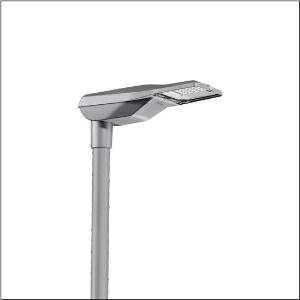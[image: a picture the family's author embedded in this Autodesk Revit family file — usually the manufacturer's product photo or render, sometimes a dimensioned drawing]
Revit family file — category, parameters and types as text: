
# Revit family: streetlight_sl_21_iq_micro___st1_5a_5xe1p31d08cb_2d79
name_source: partatom
category: Lighting Fixtures
units: mm (PartAtom-declared; Revit-internal decimal feet)

## family parameters
Cut with Voids When Loaded = No
Host = Face
Light Source = No
Part Type = Normal
Room Calculation Point = No
Round Connector Dimension = Use Diameter
Shared = No

## types (1)
- --- (1 x LED, 2820 lm, 19.4 W, 3000K)
    Apparent Load = 19 VA
    CIE Flux Codes = 22 53 95 100 100
    Color Rendering = 70
    Color Temperature = 3000K
    Default Elevation = 1800 mm
    Description = Streetlight SL 21 iQ micro, mast luminaire, primary light control with lens, of PMMA, primary optical cover: cover, of toughened safety glass, transparent, light distribution: ST1.5a, light emission: direct distribution, primary light characteristic: asymmetric, installation type: post-top, side-entry, LED, High Power LED, rated luminous flux: 2.820lm, luminous efficacy: 145lm/W, light colour: 730, colour temperature: 3000K, control: Auto-Match, Temp-Guard, Lumen-Switch, Night-Set, Smart-Wire, Light-Fading, Desk-Remote (wireless, voltage-free reading and setting of iQ features in the workshop via application-optimized NFC function/RFID function), optimised constant luminous flux control (CLO 2.0), pre-setting: linear dimming characteristic, mains connection: 220..240V, AC, 50/60Hz, start of lifetime: 19W, end of service life: 20W, reduction: 10W, luminaire housing, of diecast aluminium, powder-coated, Siteco® metallic grey (DB 702S), corrosivity category C5 mid according to DIN EN ISO 12944, please order mast flange separately, inclination adjustable: 0°, 5°, 10°, 15°, sealing non-destructively replaceable, multi-level sealing system, length: 528mm, width: 235mm, height: 110mm, mast flange for spigot size: 42mm (side-entry): 5XC10008XM4, 60/48mm (side-entry/post-top): 5XC10108XM2, 76/60mm (side-entry/post-top): 5XC10108XM1, protection rating (complete): IP66, insulation class (complete): insulation class II (safety insulation), certification: CE, ENEC, ENEC+, VDE, impact resistance: IK09, permissible operating ambient temperature for outdoor applications: -40..+50°C, standard-compliant lighting for roads and squares, packaging unit: 1 piece

Light Distribution: ST1.5a
    Height = 110 mm
    Lamp = 1 x LED
    Lamp Light Flux = 2820 lm
    Lamp Power = 19.4 W
    Lamp count = 1
    Length = 528 mm
    Luminous efficacy = 145 lm/W
    Manufacturer = Siteco
    ModVariant = No
    Model = 5XE1P31D08CB
    Number of Poles = 1
    OnlyDefault = Yes
    Power Factor = 1
    Product Name = Streetlight SL 21 iQ micro | ST1.5a
    Product group = mast luminaire | pylon top
    ProductGroupID = 6100
    Protection Class = Protection class II
    Protection Degree = IP 66
    RLX_Detail_Level = 1
    RLX_Emergency_Light_Flux = 0 lm
    RLX_Emergency_Type = 0
    RLX_Emergency_Type_DB = No
    RlxData = <blob elided: 102617 chars, md5=93837ec8>
    Socket = socket
    Standby Power = 0 W
    System Light Flux = 2820 lm
    System Power = 19 W
    Type Comments = factory setting: luminous flux: 100 % | dim-lin: 254 | 387 mA
    Type Image = l_1006881.jpg
    URL = http://relux.com
    VarID = @adj_107911
    Voltage = 0 V
    Weight = 0.00 kg
    Width = 235 mm

## geometry (parser evidence)
native form markers: Blend x4, Sweep x10
no freeform markers — native parametric forms only
